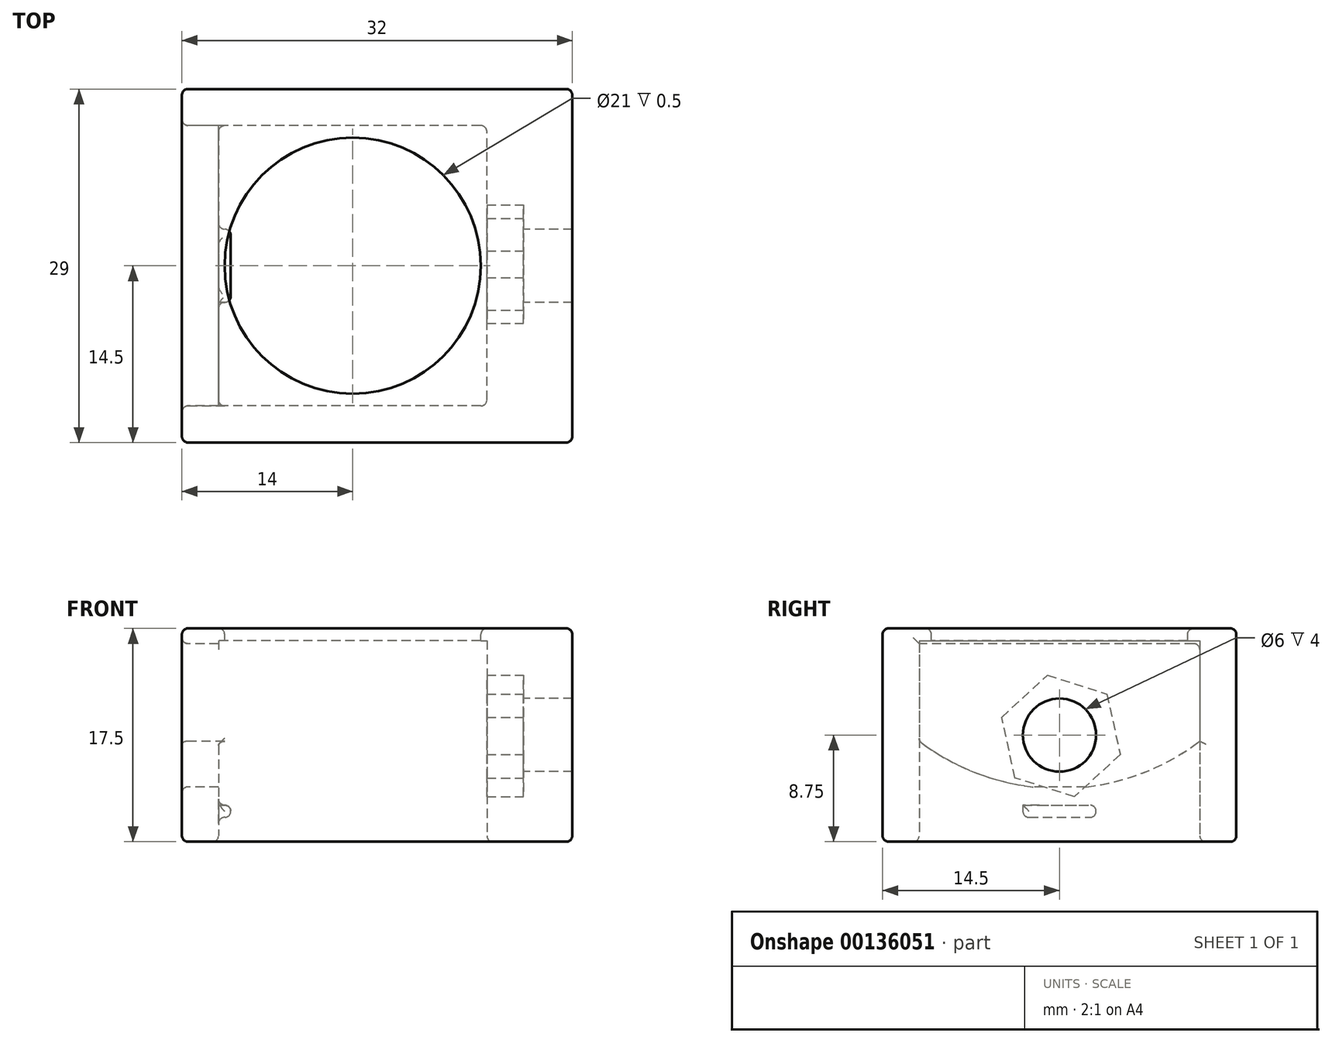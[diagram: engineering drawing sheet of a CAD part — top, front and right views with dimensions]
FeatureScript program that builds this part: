
annotation { "Feature Type Name" : "Feature", "Feature Type Description" : "" }
export const myFeature = defineFeature(function(context is Context, id is Id, definition is map)
    precondition{}
    {
        {
            var Q0;
            Q0=qCreatedBy(makeId("Top.planeOp"),FACE);
            var sketch = newSketch(context, id + "F0", { "sketchPlane" : qUnion([Q0])});
            skLineSegment(sketch, "E0.bottom", {"start": v(11, -11.5) * mm, "end": v(-11, -11.5) * mm});
            skLineSegment(sketch, "E0.top", {"start": v(11, 11.5) * mm, "end": v(-11, 11.5) * mm});
            skLineSegment(sketch, "E0.left", {"start": v(11, -11.5) * mm, "end": v(11, 11.5) * mm});
            skLineSegment(sketch, "E0.right", {"start": v(-11, -11.5) * mm, "end": v(-11, 11.5) * mm});
            skPoint(sketch, "E0.middle", {"position": v(0, 0) * mm});
            skLineSegment(sketch, "E1.0", {"start": v(14, 14.5) * mm, "end": v(-14, 14.5) * mm});
            skLineSegment(sketch, "E1.1", {"start": v(14, -14.5) * mm, "end": v(14, 14.5) * mm});
            skLineSegment(sketch, "E1.2", {"start": v(14, -14.5) * mm, "end": v(-14, -14.5) * mm});
            skLineSegment(sketch, "E1.3", {"start": v(-14, -14.5) * mm, "end": v(-14, 14.5) * mm});
            skSolve(sketch);
        }
        {
            var Q0;
            Q0=makeQuery(id+"F0.imprint","IMPRINT",FACE,{"disambiguationData":[TD([[makeQuery(id+"F0.imprint","IMPRINT",EDGE,{"derivedFrom":sQuery(id+"F0.wireOp",EDGE,"E0.bottom")}),1.0]])]});
            extrude(context, id + "F1", {"entities" : qUnion([Q0]), "depth" : 17.5 * mm});
        }
        {
            var Q0;
            Q0=makeQuery(id+"F1.opExtrude","SWEPT_FACE",FACE,{"disambiguationData":[OSD([sQuery(id+"F0.wireOp",EDGE,"E1.3")])]});
            var sketch = newSketch(context, id + "F2", { "sketchPlane" : qUnion([Q0])});
            skLineSegment(sketch, "E2.0", {"start": v(14.5, 16.5) * mm, "end": v(-14.5, 16.5) * mm});
            skLineSegment(sketch, "E3.0", {"start": v(14.5, 4.5) * mm, "end": v(-14.5, 4.5) * mm});
            skLineSegment(sketch, "E4.0", {"start": v(-11.5, 16.5) * mm, "end": v(-11.5, 0) * mm});
            skLineSegment(sketch, "E5.0", {"start": v(11.5, 16.25) * mm, "end": v(11.5, 0) * mm});
            skPoint(sketch, "E6.oppositeSnap0", {"position": v(-11.5, 8.25) * mm});
            skLineSegment(sketch, "E6.bottom", {"start": v(11.5, 16.25) * mm, "end": v(-11.5, 16.25) * mm});
            skLineSegment(sketch, "E6.top", {"start": v(11.5, 8.25) * mm, "end": v(-11.5, 8.25) * mm});
            skLineSegment(sketch, "E6.left", {"start": v(11.5, 16.25) * mm, "end": v(11.5, 8.25) * mm});
            skLineSegment(sketch, "E6.right", {"start": v(-11.5, 16.25) * mm, "end": v(-11.5, 8.25) * mm});
            skArc(sketch, "E7", {"start": v(-11.5, 8.25) * mm, "mid": v(0, 4.37) * mm, "end": v(11.5, 8.25) * mm});
            skSolve(sketch);
        }
        {
            var Q0;
            Q0=makeQuery(id+"F2.imprint","IMPRINT",FACE,{"disambiguationData":[TD([[makeQuery(id+"F2.imprint","IMPRINT",EDGE,{"derivedFrom":sQuery(id+"F2.wireOp",EDGE,"E6.bottom")}),1.0]])]});
            var Q1;
            {var subQ4=sQuery(id+"F2.wireOp",EDGE,"E6.top");Q1=makeQuery(id+"F2.imprint","IMPRINT",FACE,{"disambiguationData":[TD([[makeQuery(id+"F2.imprint","IMPRINT",EDGE,{"derivedFrom":subQ4}),1.0]])]});}
            extrude(context, id + "F3", {"entities" : qUnion([Q0, Q1]), "operationType" : NewBodyOperationType.REMOVE, "endBound" : BoundingType.UP_TO_NEXT, "oppositeDirection" : true, "depth" : 25 * mm});
        }
        {
            var Q0;
            Q0=makeQuery(id+"F1.opExtrude","SWEPT_EDGE",EDGE,{"disambiguationData":[OSD([sQuery(id+"F0.wireOp",EDGE,"E0.top"),sQuery(id+"F0.wireOp",EDGE,"E0.left")])]});
            var Q1;
            Q1=makeQuery(id+"F1.opExtrude","SWEPT_EDGE",EDGE,{"disambiguationData":[OSD([sQuery(id+"F0.wireOp",EDGE,"E0.bottom"),sQuery(id+"F0.wireOp",EDGE,"E0.left")])]});
            var Q2;
            {var subQ0=sQuery(id+"F0.wireOp",EDGE,"E0.right");var subQ1=sQuery(id+"F0.wireOp",EDGE,"E0.top");Q2=makeQuery(id+"F3.boolean.opBoolean","SPLIT",EDGE,{"disambiguationData":[TD([makeQuery(id+"F3.opExtrude","SWEPT_FACE",FACE,{"disambiguationData":[OSD([sQuery(id+"F2.wireOp",EDGE,"E3.0")])]})])],"derivedFrom":makeQuery(id+"F1.opExtrude","SWEPT_EDGE",EDGE,{"disambiguationData":[OSD([subQ1,subQ0])]})});}
            var Q3;
            {var subQ0=sQuery(id+"F0.wireOp",EDGE,"E0.right");var subQ1=sQuery(id+"F0.wireOp",EDGE,"E0.top");Q3=makeQuery(id+"F3.boolean.opBoolean","SPLIT",EDGE,{"disambiguationData":[TD([makeQuery(id+"F3.opExtrude","SWEPT_FACE",FACE,{"disambiguationData":[OSD([sQuery(id+"F2.wireOp",EDGE,"E2.0")])]})])],"derivedFrom":makeQuery(id+"F1.opExtrude","SWEPT_EDGE",EDGE,{"disambiguationData":[OSD([subQ1,subQ0])]})});}
            var Q4;
            {var subQ0=sQuery(id+"F0.wireOp",EDGE,"E0.right");var subQ1=sQuery(id+"F0.wireOp",EDGE,"E0.bottom");Q4=makeQuery(id+"F3.boolean.opBoolean","SPLIT",EDGE,{"disambiguationData":[TD([makeQuery(id+"F3.opExtrude","SWEPT_FACE",FACE,{"disambiguationData":[OSD([sQuery(id+"F2.wireOp",EDGE,"E2.0")])]})])],"derivedFrom":makeQuery(id+"F1.opExtrude","SWEPT_EDGE",EDGE,{"disambiguationData":[OSD([subQ1,subQ0])]})});}
            var Q5;
            {var subQ0=sQuery(id+"F0.wireOp",EDGE,"E0.right");var subQ1=sQuery(id+"F0.wireOp",EDGE,"E0.bottom");Q5=makeQuery(id+"F3.boolean.opBoolean","SPLIT",EDGE,{"disambiguationData":[TD([makeQuery(id+"F3.opExtrude","SWEPT_FACE",FACE,{"disambiguationData":[OSD([sQuery(id+"F2.wireOp",EDGE,"E3.0")])]})])],"derivedFrom":makeQuery(id+"F1.opExtrude","SWEPT_EDGE",EDGE,{"disambiguationData":[OSD([subQ1,subQ0])]})});}
            var Q6;
            Q6=makeQuery(id+"F3.boolean.opBoolean","COPY",EDGE,{"derivedFrom":makeQuery(id+"F3.opExtrude","CAP_EDGE",EDGE,{"disambiguationData":[OSD([sQuery(id+"F2.wireOp",EDGE,"E5.0")])],"isStart":true})});
            var Q7;
            Q7=makeQuery(id+"F3.boolean.opBoolean","COPY",EDGE,{"derivedFrom":makeQuery(id+"F3.opExtrude","CAP_EDGE",EDGE,{"disambiguationData":[OSD([sQuery(id+"F2.wireOp",EDGE,"E3.0")])],"isStart":true})});
            var Q8;
            Q8=makeQuery(id+"F3.boolean.opBoolean","COPY",EDGE,{"derivedFrom":makeQuery(id+"F3.opExtrude","CAP_EDGE",EDGE,{"disambiguationData":[OSD([sQuery(id+"F2.wireOp",EDGE,"E4.0")])],"isStart":true})});
            var Q9;
            Q9=makeQuery(id+"F3.boolean.opBoolean","COPY",EDGE,{"derivedFrom":makeQuery(id+"F3.opExtrude","CAP_EDGE",EDGE,{"disambiguationData":[OSD([sQuery(id+"F2.wireOp",EDGE,"E2.0")])],"isStart":true})});
            var Q10;
            {var subQ0=sQuery(id+"F2.wireOp",EDGE,"E7");var subQ1=sQuery(id+"F2.wireOp",EDGE,"E3.0");Q10=qUnion([makeQuery(id+"F3.boolean.opBoolean","COPY",EDGE,{"derivedFrom":makeQuery(id+"F3.opExtrude","SWEPT_EDGE",EDGE,{"disambiguationData":[OSD([subQ1,subQ0]),TDD([makeQuery(id+"F2.imprint","INTERSECT",VERTEX,{"disambiguationData":[OD(0.0)],"derivedFrom":[subQ1,subQ0]})])]})}),makeQuery(id+"F3.boolean.opBoolean","COPY",EDGE,{"derivedFrom":makeQuery(id+"F3.opExtrude","SWEPT_EDGE",EDGE,{"disambiguationData":[OSD([subQ1,subQ0]),TDD([makeQuery(id+"F2.imprint","INTERSECT",VERTEX,{"disambiguationData":[OD(1.0)],"derivedFrom":[subQ1,subQ0]})])]})})]);}
            var Q11;
            {var subQ0=sQuery(id+"F2.wireOp",EDGE,"E7");var subQ1=sQuery(id+"F2.wireOp",EDGE,"E3.0");Q11=qUnion([makeQuery(id+"F3.boolean.opBoolean","COPY",EDGE,{"derivedFrom":makeQuery(id+"F3.opExtrude","SWEPT_EDGE",EDGE,{"disambiguationData":[OSD([subQ1,subQ0]),TDD([makeQuery(id+"F2.imprint","INTERSECT",VERTEX,{"disambiguationData":[OD(0.0)],"derivedFrom":[subQ1,subQ0]})])]})}),makeQuery(id+"F3.boolean.opBoolean","COPY",EDGE,{"derivedFrom":makeQuery(id+"F3.opExtrude","SWEPT_EDGE",EDGE,{"disambiguationData":[OSD([subQ1,subQ0]),TDD([makeQuery(id+"F2.imprint","INTERSECT",VERTEX,{"disambiguationData":[OD(1.0)],"derivedFrom":[subQ1,subQ0]})])]})})]);}
            var Q12;
            Q12=makeQuery(id+"F3.boolean.opBoolean","COPY",EDGE,{"derivedFrom":makeQuery(id+"F3.opExtrude","SWEPT_EDGE",EDGE,{"disambiguationData":[OSD([sQuery(id+"F2.wireOp",EDGE,"E5.0"),sQuery(id+"F2.wireOp",EDGE,"E6.top"),sQuery(id+"F2.wireOp",EDGE,"E6.left"),sQuery(id+"F2.wireOp",EDGE,"E7")])]})});
            var Q13;
            Q13=makeQuery(id+"F3.boolean.opBoolean","COPY",EDGE,{"derivedFrom":makeQuery(id+"F3.opExtrude","SWEPT_EDGE",EDGE,{"disambiguationData":[OSD([sQuery(id+"F2.wireOp",EDGE,"E4.0"),sQuery(id+"F2.wireOp",EDGE,"E6.bottom"),sQuery(id+"F2.wireOp",EDGE,"E6.right")])]})});
            var Q14;
            {var subQ0=sQuery(id+"F2.wireOp",EDGE,"E7");Q14=makeQuery(id+"F3.boolean.opBoolean","COPY",EDGE,{"derivedFrom":makeQuery(id+"F3.opExtrude","CAP_EDGE",EDGE,{"disambiguationData":[OSD([subQ0]),TDD([makeQuery(id+"F2.imprint","IMPRINT",EDGE,{"disambiguationData":[TD([[makeQuery(id+"F2.imprint","INTERSECT",VERTEX,{"disambiguationData":[OD(0.0)],"derivedFrom":[sQuery(id+"F2.wireOp",EDGE,"E3.0"),subQ0]}),-1.0]])],"derivedFrom":subQ0})])],"isStart":false})});}
            var Q15;
            {var subQ1=sQuery(id+"F0.wireOp",EDGE,"E0.right");var subQ2=sQuery(id+"F0.wireOp",EDGE,"E0.bottom");var subQ3=sQuery(id+"F2.wireOp",EDGE,"E7");Q15=makeQuery(id+"F3.boolean.opBoolean","SPLIT",EDGE,{"disambiguationData":[TD([makeQuery(id+"F3.opExtrude","SWEPT_FACE",FACE,{"disambiguationData":[OSD([subQ3]),TDD([makeQuery(id+"F2.imprint","IMPRINT",EDGE,{"disambiguationData":[TD([[makeQuery(id+"F2.imprint","INTERSECT",VERTEX,{"disambiguationData":[OD(0.0)],"derivedFrom":[sQuery(id+"F2.wireOp",EDGE,"E3.0"),subQ3]}),-1.0]])],"derivedFrom":subQ3})])]})])],"derivedFrom":makeQuery(id+"F1.opExtrude","SWEPT_EDGE",EDGE,{"disambiguationData":[OSD([subQ2,subQ1])]})});}
            var Q16;
            {var subQ0=sQuery(id+"F0.wireOp",EDGE,"E0.right");var subQ2=sQuery(id+"F0.wireOp",EDGE,"E0.top");var subQ3=sQuery(id+"F2.wireOp",EDGE,"E7");Q16=makeQuery(id+"F3.boolean.opBoolean","SPLIT",EDGE,{"disambiguationData":[TD([makeQuery(id+"F3.opExtrude","SWEPT_FACE",FACE,{"disambiguationData":[OSD([subQ3]),TDD([makeQuery(id+"F2.imprint","IMPRINT",EDGE,{"disambiguationData":[TD([[makeQuery(id+"F2.imprint","INTERSECT",VERTEX,{"disambiguationData":[OD(1.0)],"derivedFrom":[sQuery(id+"F2.wireOp",EDGE,"E3.0"),subQ3]}),1.0]])],"derivedFrom":subQ3})])]})])],"derivedFrom":makeQuery(id+"F1.opExtrude","SWEPT_EDGE",EDGE,{"disambiguationData":[OSD([subQ2,subQ0])]})});}
            var Q17;
            Q17=makeQuery(id+"F1.opExtrude","CAP_EDGE",EDGE,{"disambiguationData":[OSD([sQuery(id+"F0.wireOp",EDGE,"E1.3")])],"isStart":true});
            var Q18;
            Q18=makeQuery(id+"F1.opExtrude","SWEPT_EDGE",EDGE,{"disambiguationData":[OSD([sQuery(id+"F0.wireOp",EDGE,"E1.0"),sQuery(id+"F0.wireOp",EDGE,"E1.3")])]});
            var Q19;
            Q19=makeQuery(id+"F1.opExtrude","CAP_EDGE",EDGE,{"disambiguationData":[OSD([sQuery(id+"F0.wireOp",EDGE,"E1.0")])],"isStart":true});
            var Q20;
            Q20=makeQuery(id+"F1.opExtrude","CAP_EDGE",EDGE,{"disambiguationData":[OSD([sQuery(id+"F0.wireOp",EDGE,"E1.2")])],"isStart":true});
            var Q21;
            Q21=makeQuery(id+"F1.opExtrude","CAP_EDGE",EDGE,{"disambiguationData":[OSD([sQuery(id+"F0.wireOp",EDGE,"E1.2")])],"isStart":false});
            var Q22;
            Q22=makeQuery(id+"F1.opExtrude","SWEPT_EDGE",EDGE,{"disambiguationData":[OSD([sQuery(id+"F0.wireOp",EDGE,"E1.2"),sQuery(id+"F0.wireOp",EDGE,"E1.3")])]});
            var Q23;
            Q23=makeQuery(id+"F1.opExtrude","CAP_EDGE",EDGE,{"disambiguationData":[OSD([sQuery(id+"F0.wireOp",EDGE,"E0.left")])],"isStart":true});
            var Q24;
            Q24=makeQuery(id+"F1.opExtrude","CAP_EDGE",EDGE,{"disambiguationData":[OSD([sQuery(id+"F0.wireOp",EDGE,"E0.bottom")])],"isStart":true});
            var Q25;
            Q25=makeQuery(id+"F1.opExtrude","CAP_EDGE",EDGE,{"disambiguationData":[OSD([sQuery(id+"F0.wireOp",EDGE,"E0.top")])],"isStart":false});
            var Q26;
            Q26=makeQuery(id+"F1.opExtrude","CAP_EDGE",EDGE,{"disambiguationData":[OSD([sQuery(id+"F0.wireOp",EDGE,"E0.right")])],"isStart":false});
            fillet(context, id + "F4", {"entities" : qUnion([Q0, Q1, Q2, Q3, Q4, Q5, Q6, Q7, Q8, Q9, Q10, Q11, Q12, Q13, Q14, Q15, Q16, Q17, Q18, Q19, Q20, Q21, Q22, Q23, Q24, Q25, Q26]), "radius" : .5 * mm, "tangentPropagation" : true, "allowEdgeOverflow" : false});
        }
        {
            var Q0;
            Q0=makeQuery(id+"F1.opExtrude","CAP_FACE",FACE,{"disambiguationData":[OSD([sQuery(id+"F0.wireOp",EDGE,"E0.bottom"),sQuery(id+"F0.wireOp",EDGE,"E0.top"),sQuery(id+"F0.wireOp",EDGE,"E0.left"),sQuery(id+"F0.wireOp",EDGE,"E0.right"),sQuery(id+"F0.wireOp",EDGE,"E1.0"),sQuery(id+"F0.wireOp",EDGE,"E1.1"),sQuery(id+"F0.wireOp",EDGE,"E1.2"),sQuery(id+"F0.wireOp",EDGE,"E1.3")])],"isStart":false});
            var sketch = newSketch(context, id + "F5", { "sketchPlane" : qUnion([Q0])});
            skCircle(sketch, "E8", {"center": v(0, 0) * mm, "radius": 10.5 * mm});
            skSolve(sketch);
        }
        {
            var Q0;
            Q0=makeQuery(id+"F5.imprint","IMPRINT",FACE,{"disambiguationData":[TD([[makeQuery(id+"F5.imprint","IMPRINT",EDGE,{"derivedFrom":sQuery(id+"F5.wireOp",EDGE,"E8")}),-1.0]])]});
            extrude(context, id + "F6", {"entities" : qUnion([Q0]), "operationType" : NewBodyOperationType.ADD, "oppositeDirection" : true, "depth" : 1 * mm});
        }
        {
            var Q0;
            Q0=makeQuery(id+"F1.opExtrude","SWEPT_FACE",FACE,{"disambiguationData":[OSD([sQuery(id+"F0.wireOp",EDGE,"E1.1")])]});
            var sketch = newSketch(context, id + "F7", { "sketchPlane" : qUnion([Q0])});
            skLineSegment(sketch, "E9", {"start": v(-14.5, 0) * mm, "end": v(14.5, 17.5) * mm, "construction": true});
            skLineSegment(sketch, "E10", {"start": v(14.5, 0) * mm, "end": v(-14.5, 17.5) * mm, "construction": true});
            skCircle(sketch, "E11", {"center": v(0, 8.75) * mm, "radius": 3 * mm});
            skLineSegment(sketch, "E12.0", {"start": v(-0.98, 13.65) * mm, "end": v(3.88, 12.12) * mm});
            skLineSegment(sketch, "E12.1", {"start": v(3.88, 12.12) * mm, "end": v(4.98, 7.15) * mm});
            skLineSegment(sketch, "E12.2", {"start": v(4.98, 7.15) * mm, "end": v(1.23, 3.7) * mm});
            skLineSegment(sketch, "E12.3", {"start": v(1.23, 3.7) * mm, "end": v(-3.64, 5.23) * mm});
            skLineSegment(sketch, "E12.4", {"start": v(-3.64, 5.23) * mm, "end": v(-4.74, 10.2) * mm});
            skLineSegment(sketch, "E12.5", {"start": v(-4.74, 10.2) * mm, "end": v(-0.98, 13.65) * mm});
            skSolve(sketch);
        }
        {
            var Q0;
            Q0=makeQuery(id+"F1.opExtrude","SWEPT_FACE",FACE,{"disambiguationData":[OSD([sQuery(id+"F0.wireOp",EDGE,"E1.1")])]});
            extrude(context, id + "F8", {"entities" : qUnion([Q0]), "operationType" : NewBodyOperationType.ADD, "depth" : 4 * mm});
        }
        {
            var Q0;
            Q0=makeQuery(id+"F1.opExtrude","CAP_EDGE",EDGE,{"disambiguationData":[OSD([sQuery(id+"F0.wireOp",EDGE,"E1.3")])],"isStart":true});
            var Q1;
            Q1=makeQuery(id+"F1.opExtrude","SWEPT_EDGE",EDGE,{"disambiguationData":[OSD([sQuery(id+"F0.wireOp",EDGE,"E1.2"),sQuery(id+"F0.wireOp",EDGE,"E1.3")])]});
            var Q2;
            {var subQ0=sQuery(id+"F0.wireOp",EDGE,"E1.2");Q2=makeQuery(id+"F8.boolean.opBoolean","MERGE",FACE,{"derivedFrom":[makeQuery(id+"F1.opExtrude","SWEPT_FACE",FACE,{"disambiguationData":[OSD([subQ0])]}),makeQuery(id+"F8.opExtrude","SWEPT_FACE",FACE,{"disambiguationData":[OSD([sQuery(id+"F0.wireOp",EDGE,"E1.1"),subQ0])]})]});}
            var Q3;
            {var subQ0=sQuery(id+"F0.wireOp",EDGE,"E1.1");Q3=makeQuery(id+"F8.boolean.opBoolean","MERGE",FACE,{"derivedFrom":[makeQuery(id+"F1.opExtrude","CAP_FACE",FACE,{"disambiguationData":[OSD([sQuery(id+"F0.wireOp",EDGE,"E0.bottom"),sQuery(id+"F0.wireOp",EDGE,"E0.top"),sQuery(id+"F0.wireOp",EDGE,"E0.left"),sQuery(id+"F0.wireOp",EDGE,"E0.right"),sQuery(id+"F0.wireOp",EDGE,"E1.0"),subQ0,sQuery(id+"F0.wireOp",EDGE,"E1.2"),sQuery(id+"F0.wireOp",EDGE,"E1.3")])],"isStart":true}),makeQuery(id+"F8.opExtrude","SWEPT_FACE",FACE,{"disambiguationData":[OSD([subQ0]),TDD([makeQuery(id+"F1.opExtrude","CAP_EDGE",EDGE,{"disambiguationData":[OSD([subQ0])],"isStart":true})])]})]});}
            var Q4;
            Q4=makeQuery(id+"F1.opExtrude","SWEPT_FACE",FACE,{"disambiguationData":[OSD([sQuery(id+"F0.wireOp",EDGE,"E1.3")])]});
            var Q5;
            {var subQ0=sQuery(id+"F0.wireOp",EDGE,"E1.0");Q5=makeQuery(id+"F8.boolean.opBoolean","MERGE",FACE,{"derivedFrom":[makeQuery(id+"F1.opExtrude","SWEPT_FACE",FACE,{"disambiguationData":[OSD([subQ0])]}),makeQuery(id+"F8.opExtrude","SWEPT_FACE",FACE,{"disambiguationData":[OSD([subQ0,sQuery(id+"F0.wireOp",EDGE,"E1.1")])]})]});}
            var Q6;
            Q6=makeQuery(id+"F8.opExtrude","CAP_FACE",FACE,{"disambiguationData":[OSD([sQuery(id+"F0.wireOp",EDGE,"E1.1")])],"isStart":false});
            var Q7;
            {var subQ0=sQuery(id+"F0.wireOp",EDGE,"E1.1");var subQ1=sQuery(id+"F0.wireOp",EDGE,"E1.3");var subQ2=sQuery(id+"F0.wireOp",EDGE,"E1.2");var subQ3=sQuery(id+"F0.wireOp",EDGE,"E1.0");var subQ4=sQuery(id+"F0.wireOp",EDGE,"E0.right");var subQ5=sQuery(id+"F0.wireOp",EDGE,"E0.left");var subQ6=sQuery(id+"F0.wireOp",EDGE,"E0.top");var subQ7=sQuery(id+"F0.wireOp",EDGE,"E0.bottom");Q7=makeQuery(id+"F8.boolean.opBoolean","MERGE",FACE,{"derivedFrom":[makeQuery(id+"F6.boolean.opBoolean","MERGE",FACE,{"derivedFrom":[makeQuery(id+"F1.opExtrude","CAP_FACE",FACE,{"disambiguationData":[OSD([subQ7,subQ6,subQ5,subQ4,subQ3,subQ0,subQ2,subQ1])],"isStart":false}),makeQuery(id+"F6.opExtrude","CAP_FACE",FACE,{"disambiguationData":[OSD([subQ7,subQ6,subQ5,subQ4,subQ3,subQ0,subQ2,subQ1,sQuery(id+"F5.wireOp",EDGE,"E8")])],"isStart":true})]}),makeQuery(id+"F8.opExtrude","SWEPT_FACE",FACE,{"disambiguationData":[OSD([subQ0]),TDD([makeQuery(id+"F1.opExtrude","CAP_EDGE",EDGE,{"disambiguationData":[OSD([subQ0])],"isStart":false})])]})]});}
            fillet(context, id + "F9", {"entities" : qUnion([Q0, Q1, Q2, Q3, Q4, Q5, Q6, Q7]), "radius" : .5 * mm, "tangentPropagation" : true, "allowEdgeOverflow" : false});
        }
        {
            var Q0;
            {var subQ0=sQuery(id+"F2.wireOp",EDGE,"E3.0");var subQ1=sQuery(id+"F0.wireOp",EDGE,"E0.right");Q0=makeQuery(id+"F3.boolean.opBoolean","SPLIT",FACE,{"disambiguationData":[TD([makeQuery(id+"F3.opExtrude","SWEPT_FACE",FACE,{"disambiguationData":[OSD([subQ0])]})])],"derivedFrom":makeQuery(id+"F1.opExtrude","SWEPT_FACE",FACE,{"disambiguationData":[OSD([subQ1])]})});}
            var sketch = newSketch(context, id + "F10", { "sketchPlane" : qUnion([Q0])});
            skLineSegment(sketch, "E13.bottom", {"start": v(-3, 3) * mm, "end": v(3, 3) * mm});
            skLineSegment(sketch, "E13.top", {"start": v(-3, 2) * mm, "end": v(3, 2) * mm});
            skLineSegment(sketch, "E13.left", {"start": v(-3, 3) * mm, "end": v(-3, 2) * mm});
            skLineSegment(sketch, "E13.right", {"start": v(3, 3) * mm, "end": v(3, 2) * mm});
            skPoint(sketch, "E13.middle", {"position": v(0, 2.5) * mm});
            skSolve(sketch);
        }
        {
            var Q0;
            Q0 = qSketchRegion(id + "F10", true);
            var Q1;
            Q1=makeQuery(id+"F10.imprint","IMPRINT",FACE,{"disambiguationData":[TD([[makeQuery(id+"F10.imprint","IMPRINT",EDGE,{"derivedFrom":sQuery(id+"F10.wireOp",EDGE,"E13.bottom")}),-1.0]])]});
            extrude(context, id + "F11", {"entities" : qUnion([Q0, Q1]), "operationType" : NewBodyOperationType.ADD, "depth" : 1 * mm});
        }
        {
            var Q0;
            Q0=makeQuery(id+"F11.opExtrude","CAP_FACE",FACE,{"disambiguationData":[OSD([sQuery(id+"F10.wireOp",EDGE,"E13.bottom"),sQuery(id+"F10.wireOp",EDGE,"E13.top"),sQuery(id+"F10.wireOp",EDGE,"E13.left"),sQuery(id+"F10.wireOp",EDGE,"E13.right")])],"isStart":false});
            var Q1;
            Q1=makeQuery(id+"F11.opExtrude","CAP_EDGE",EDGE,{"disambiguationData":[OSD([sQuery(id+"F10.wireOp",EDGE,"E13.top")])],"isStart":false});
            var Q2;
            Q2=makeQuery(id+"F11.opExtrude","SWEPT_FACE",FACE,{"disambiguationData":[OSD([sQuery(id+"F10.wireOp",EDGE,"E13.top")])]});
            var Q3;
            Q3=makeQuery(id+"F11.opExtrude","SWEPT_FACE",FACE,{"disambiguationData":[OSD([sQuery(id+"F10.wireOp",EDGE,"E13.right")])]});
            fillet(context, id + "F12", {"entities" : qUnion([Q0, Q1, Q2, Q3]), "radius" : .5 * mm, "tangentPropagation" : true, "allowEdgeOverflow" : false});
        }
        {
            var Q0;
            Q0=makeQuery(id+"FoewKxR6trpoF0O_1.boolean.opBoolean","SPLIT",FACE,{"disambiguationData":[TD([makeQuery(id+"FoewKxR6trpoF0O_1.opExtrude","SWEPT_FACE",FACE,{"disambiguationData":[OSD([sQuery(id+"F7.wireOp",EDGE,"E11")])]})])],"derivedFrom":makeQuery(id+"F1.opExtrude","SWEPT_FACE",FACE,{"disambiguationData":[OSD([sQuery(id+"F0.wireOp",EDGE,"E0.left")])]})});
            var sketch = newSketch(context, id + "F13", { "sketchPlane" : qUnion([Q0])});
            skCircle(sketch, "E14", {"center": v(0, 8.75) * mm, "radius": 3 * mm});
            skSolve(sketch);
        }
        {
            var Q0;
            Q0 = qSketchRegion(id + "F13", true);
            extrude(context, id + "F14", {"entities" : qUnion([Q0]), "operationType" : NewBodyOperationType.REMOVE, "endBound" : BoundingType.THROUGH_ALL, "oppositeDirection" : true, "depth" : 25 * mm});
        }
        {
            var Q0;
            Q0 = qSketchRegion(id + "F7", true);
            extrude(context, id + "F15", {"entities" : qUnion([Q0]), "operationType" : NewBodyOperationType.REMOVE, "endBound" : BoundingType.UP_TO_NEXT, "oppositeDirection" : true, "depth" : 25 * mm});
        }
    });
